# Revit family: FU_Table_Sandler_Laminar 0924
name_source: partatom
category: Furniture
units: mm (PartAtom-declared; Revit-internal decimal feet)

## family parameters
Always vertical = Yes
Cut with Voids When Loaded = No
OmniClass Number = 23.40.20.00
OmniClass Title = General Furniture and Specialties
Room Calculation Point = No
Shared = No
Work Plane-Based = No

## types (3) — shared parameters
Depth = 900 mm  [stored 2.95276 ft]
Description = 240cm x 90cm / 95″ x 36″ table on epoxy painted frame.
Manufacturer = Sandler
Model = Laminar 0924
URL = https://www.sandlerseating.com
Width = 2400 mm
zero-valued in all types: Default Elevation

## per-type parameters (varying)
| type | Height |
| Laminar 0924 (Dining Height) | 750 mm  [stored 2.46063 ft] |
| Laminar 0924 (Counter Height) | 900 mm  [stored 2.95276 ft] |
| Laminar 0924 (Bar Height) | 1050 mm |

note: [stored X ft] marks values corroborated as IEEE doubles in the binary element streams (Revit-internal decimal feet)

## geometry (parser evidence)
native form markers: Sweep x3
no freeform markers — native parametric forms only
